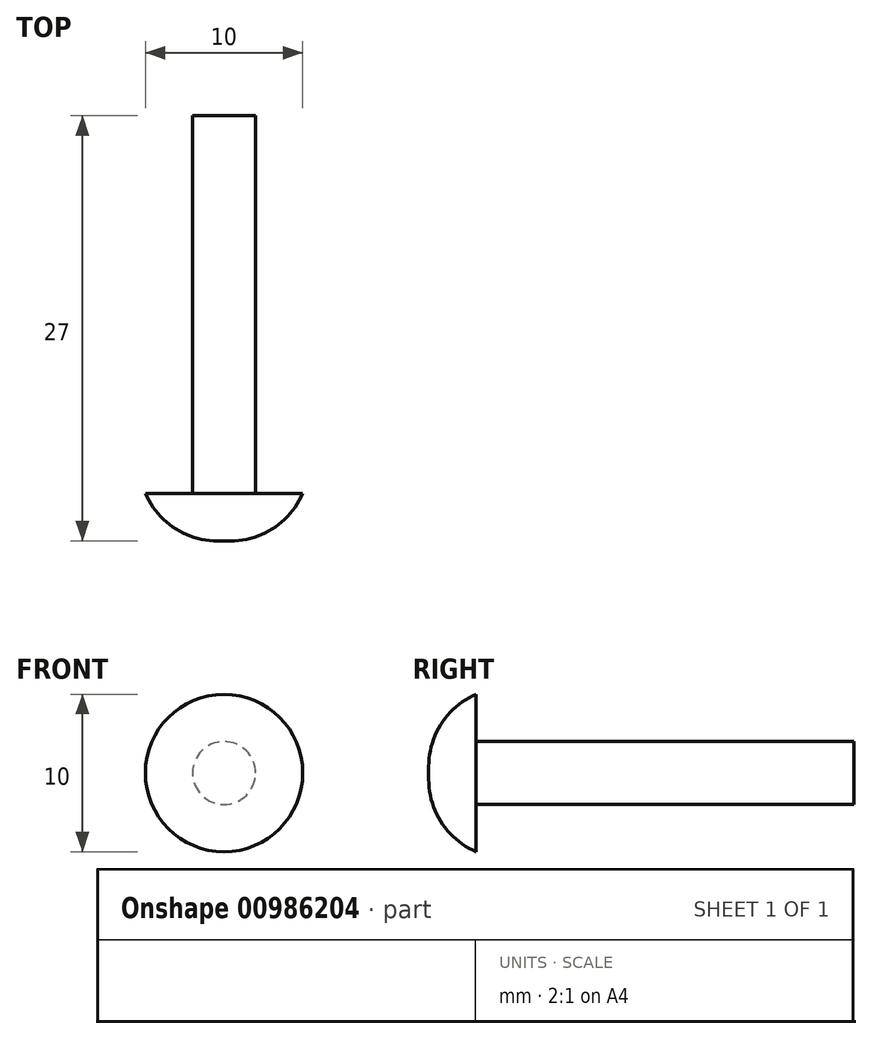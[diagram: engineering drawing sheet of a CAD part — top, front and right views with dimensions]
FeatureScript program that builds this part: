
annotation { "Feature Type Name" : "Feature", "Feature Type Description" : "" }
export const myFeature = defineFeature(function(context is Context, id is Id, definition is map)
    precondition{}
    {
        {
            var Q0;
            Q0=qCreatedBy(makeId("Front.planeOp"),FACE);
            var sketch = newSketch(context, id + "F0", { "sketchPlane" : qUnion([Q0])});
            skCircle(sketch, "E0", {"center": v(0, 0) * mm, "radius": 2 * mm});
            skSolve(sketch);
        }
        {
            var Q0;
            Q0 = qSketchRegion(id + "F0", true);
            extrude(context, id + "F1", {"entities" : qUnion([Q0]), "depth" : 24 * mm, "offsetDistance" : 25 * mm});
        }
        {
            var Q0;
            Q0=makeQuery(id+"F1.opExtrude","CAP_FACE",FACE,{"disambiguationData":[OSD([sQuery(id+"F0.wireOp",EDGE,"E0")])],"isStart":false});
            var sketch = newSketch(context, id + "F2", { "sketchPlane" : qUnion([Q0])});
            skCircle(sketch, "E1", {"center": v(0, 0) * mm, "radius": 5 * mm});
            skSolve(sketch);
        }
        {
            var Q0;
            Q0=makeQuery(id+"F2.imprint","IMPRINT",FACE,{"disambiguationData":[TD([[makeQuery(id+"F2.imprint","IMPRINT",EDGE,{"derivedFrom":makeQuery(id+"F1.opExtrude","CAP_EDGE",EDGE,{"disambiguationData":[OSD([sQuery(id+"F0.wireOp",EDGE,"E0")])],"isStart":false})}),1.0]])]});
            var Q1;
            Q1=makeQuery(id+"F2.imprint","IMPRINT",FACE,{"disambiguationData":[TD([[makeQuery(id+"F2.imprint","IMPRINT",EDGE,{"derivedFrom":sQuery(id+"F2.wireOp",EDGE,"E1")}),1.0]])]});
            extrude(context, id + "F3", {"entities" : qUnion([Q0, Q1]), "operationType" : NewBodyOperationType.ADD, "depth" : 3 * mm, "offsetDistance" : 25 * mm});
        }
        {
            var Q0;
            Q0=makeQuery(id+"F3.opExtrude","CAP_EDGE",EDGE,{"disambiguationData":[OSD([sQuery(id+"F2.wireOp",EDGE,"E1")])],"isStart":false});
            fillet(context, id + "F4", {"entities" : qUnion([Q0]), "radius" : 5 * mm, "tangentPropagation" : true, "allowEdgeOverflow" : false});
        }
    });
